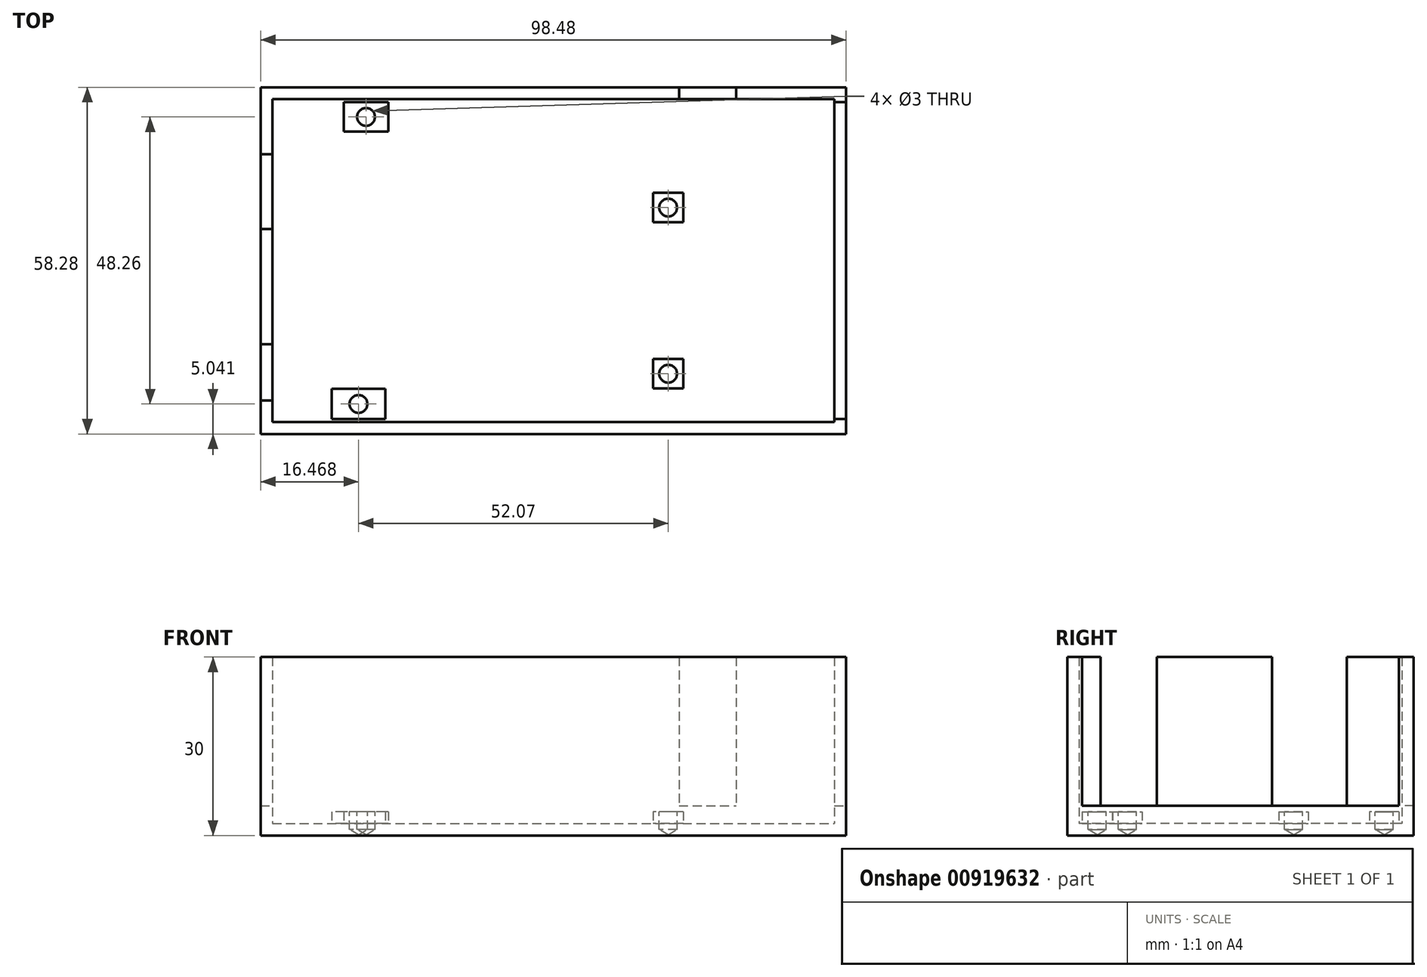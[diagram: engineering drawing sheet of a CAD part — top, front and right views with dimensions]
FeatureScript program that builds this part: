
annotation { "Feature Type Name" : "Feature", "Feature Type Description" : "" }
export const myFeature = defineFeature(function(context is Context, id is Id, definition is map)
    precondition{}
    {
        {
            var Q0;
            Q0=qCreatedBy(makeId("Top.planeOp"),FACE);
            var sketch = newSketch(context, id + "F0", { "sketchPlane" : qUnion([Q0])});
            skLineSegment(sketch, "E0.bottom", {"start": v(-55.82, 21.85) * mm, "end": v(38.66, 21.85) * mm});
            skLineSegment(sketch, "E0.top", {"start": v(-55.82, -32.43) * mm, "end": v(38.66, -32.43) * mm});
            skLineSegment(sketch, "E0.left", {"start": v(-55.82, 21.85) * mm, "end": v(-55.82, -32.43) * mm});
            skLineSegment(sketch, "E0.right", {"start": v(38.66, 21.85) * mm, "end": v(38.66, -32.43) * mm});
            skLineSegment(sketch, "E1.0", {"start": v(-57.82, 23.85) * mm, "end": v(40.66, 23.85) * mm});
            skLineSegment(sketch, "E1.1", {"start": v(-57.82, 23.85) * mm, "end": v(-57.82, -34.43) * mm});
            skLineSegment(sketch, "E1.2", {"start": v(-57.82, -34.43) * mm, "end": v(40.66, -34.43) * mm});
            skLineSegment(sketch, "E1.3", {"start": v(40.66, 23.85) * mm, "end": v(40.66, -34.43) * mm});
            skLineSegment(sketch, "E2", {"start": v(-57.82, 12.6) * mm, "end": v(-55.82, 12.6) * mm});
            skLineSegment(sketch, "E3", {"start": v(-57.82, 0) * mm, "end": v(-55.82, 0) * mm});
            skLineSegment(sketch, "E4", {"start": v(-57.82, -19.35) * mm, "end": v(-55.82, -19.35) * mm});
            skLineSegment(sketch, "E5", {"start": v(-57.82, -28.82) * mm, "end": v(-55.82, -28.82) * mm});
            skLineSegment(sketch, "E6", {"start": v(12.55, 23.85) * mm, "end": v(12.55, 21.85) * mm});
            skLineSegment(sketch, "E7", {"start": v(22.14, 21.85) * mm, "end": v(22.14, 23.85) * mm});
            skLineSegment(sketch, "E8", {"start": v(38.66, 21.35) * mm, "end": v(40.66, 21.35) * mm});
            skLineSegment(sketch, "E9", {"start": v(38.66, -31.93) * mm, "end": v(40.66, -31.93) * mm});
            skPoint(sketch, "E10", {"position": v(-40.08, 18.87) * mm});
            skLineSegment(sketch, "E11.bottom", {"start": v(-36.31, 21.35) * mm, "end": v(-43.85, 21.35) * mm});
            skLineSegment(sketch, "E11.top", {"start": v(-36.31, 16.4) * mm, "end": v(-43.85, 16.4) * mm});
            skLineSegment(sketch, "E11.left", {"start": v(-36.31, 21.35) * mm, "end": v(-36.31, 16.4) * mm});
            skLineSegment(sketch, "E11.right", {"start": v(-43.85, 21.35) * mm, "end": v(-43.85, 16.4) * mm});
            skPoint(sketch, "E12", {"position": v(-41.35, -29.39) * mm});
            skLineSegment(sketch, "E13.bottom", {"start": v(-36.84, -31.93) * mm, "end": v(-45.86, -31.93) * mm});
            skLineSegment(sketch, "E13.top", {"start": v(-36.84, -26.85) * mm, "end": v(-45.86, -26.85) * mm});
            skLineSegment(sketch, "E13.left", {"start": v(-36.84, -31.93) * mm, "end": v(-36.84, -26.85) * mm});
            skLineSegment(sketch, "E13.right", {"start": v(-45.86, -31.93) * mm, "end": v(-45.86, -26.85) * mm});
            skPoint(sketch, "E14", {"position": v(10.72, 3.63) * mm});
            skPoint(sketch, "E15", {"position": v(10.72, -24.3) * mm});
            skLineSegment(sketch, "E16.bottom", {"start": v(13.26, 1.14) * mm, "end": v(8.18, 1.14) * mm});
            skLineSegment(sketch, "E16.top", {"start": v(13.26, 6.12) * mm, "end": v(8.18, 6.12) * mm});
            skLineSegment(sketch, "E16.left", {"start": v(13.26, 1.14) * mm, "end": v(13.26, 6.12) * mm});
            skLineSegment(sketch, "E16.right", {"start": v(8.18, 1.14) * mm, "end": v(8.18, 6.12) * mm});
            skLineSegment(sketch, "E17.bottom", {"start": v(13.26, -26.8) * mm, "end": v(8.18, -26.8) * mm});
            skLineSegment(sketch, "E17.top", {"start": v(13.26, -21.82) * mm, "end": v(8.18, -21.82) * mm});
            skLineSegment(sketch, "E17.left", {"start": v(13.26, -26.8) * mm, "end": v(13.26, -21.82) * mm});
            skLineSegment(sketch, "E17.right", {"start": v(8.18, -26.8) * mm, "end": v(8.18, -21.82) * mm});
            skSolve(sketch);
        }
        {
            var Q0;
            {var subQ1=sQuery(id+"F0.wireOp",EDGE,"E0.top");Q0=makeQuery(id+"F0.imprint","IMPRINT",FACE,{"disambiguationData":[TD([[makeQuery(id+"F0.imprint","IMPRINT",EDGE,{"derivedFrom":subQ1}),1.0]])]});}
            extrude(context, id + "F1", {"entities" : qUnion([Q0]), "depth" : 2 * mm, "offsetDistance" : 25 * mm});
        }
        {
            var Q0;
            Q0=makeQuery(id+"F0.imprint","IMPRINT",FACE,{"disambiguationData":[TD([[makeQuery(id+"F0.imprint","IMPRINT",EDGE,{"derivedFrom":sQuery(id+"F0.wireOp",EDGE,"E11.bottom")}),1.0]])]});
            var Q1;
            Q1=makeQuery(id+"F0.imprint","IMPRINT",FACE,{"disambiguationData":[TD([[makeQuery(id+"F0.imprint","IMPRINT",EDGE,{"derivedFrom":sQuery(id+"F0.wireOp",EDGE,"E16.bottom")}),-1.0]])]});
            var Q2;
            Q2=makeQuery(id+"F0.imprint","IMPRINT",FACE,{"disambiguationData":[TD([[makeQuery(id+"F0.imprint","IMPRINT",EDGE,{"derivedFrom":sQuery(id+"F0.wireOp",EDGE,"E17.bottom")}),-1.0]])]});
            var Q3;
            Q3=makeQuery(id+"F0.imprint","IMPRINT",FACE,{"disambiguationData":[TD([[makeQuery(id+"F0.imprint","IMPRINT",EDGE,{"derivedFrom":sQuery(id+"F0.wireOp",EDGE,"E13.bottom")}),-1.0]])]});
            extrude(context, id + "F2", {"entities" : qUnion([Q0, Q1, Q2, Q3]), "operationType" : NewBodyOperationType.ADD, "depth" : 4 * mm, "offsetDistance" : 25 * mm});
        }
        {
            var Q0;
            Q0=makeQuery(id+"F2.opExtrude","CAP_FACE",FACE,{"disambiguationData":[OSD([sQuery(id+"F0.wireOp",EDGE,"E11.bottom"),sQuery(id+"F0.wireOp",EDGE,"E11.top"),sQuery(id+"F0.wireOp",EDGE,"E11.left"),sQuery(id+"F0.wireOp",EDGE,"E11.right")])],"isStart":false});
            var sketch = newSketch(context, id + "F3", { "sketchPlane" : qUnion([Q0])});
            skPoint(sketch, "E18.0", {"position": v(-40.08, 18.87) * mm});
            skPoint(sketch, "E19.0", {"position": v(-41.35, -29.39) * mm});
            skPoint(sketch, "E20.0", {"position": v(10.72, -24.3) * mm});
            skPoint(sketch, "E21.0", {"position": v(10.72, 3.63) * mm});
            skSolve(sketch);
        }
        {
            var Q0;
            Q0=sQuery(id+"F3.wireOp",VERTEX,"E18.0");
            var Q1;
            Q1=sQuery(id+"F3.wireOp",VERTEX,"E19.0");
            var Q2;
            Q2=sQuery(id+"F3.wireOp",VERTEX,"E20.0");
            var Q3;
            Q3=sQuery(id+"F3.wireOp",VERTEX,"E21.0");
            var Q4;
            Q4=makeQuery(id+"F1.opExtrude","SWEPT_BODY",BODY,{"disambiguationData":[OSD([sQuery(id+"F0.wireOp",EDGE,"E0.bottom"),sQuery(id+"F0.wireOp",EDGE,"E0.top"),sQuery(id+"F0.wireOp",EDGE,"E0.left"),sQuery(id+"F0.wireOp",EDGE,"E0.right"),sQuery(id+"F0.wireOp",EDGE,"E11.bottom"),sQuery(id+"F0.wireOp",EDGE,"E11.top"),sQuery(id+"F0.wireOp",EDGE,"E11.left"),sQuery(id+"F0.wireOp",EDGE,"E11.right"),sQuery(id+"F0.wireOp",EDGE,"E13.bottom"),sQuery(id+"F0.wireOp",EDGE,"E13.top"),sQuery(id+"F0.wireOp",EDGE,"E13.left"),sQuery(id+"F0.wireOp",EDGE,"E13.right"),sQuery(id+"F0.wireOp",EDGE,"E16.bottom"),sQuery(id+"F0.wireOp",EDGE,"E16.top"),sQuery(id+"F0.wireOp",EDGE,"E16.left"),sQuery(id+"F0.wireOp",EDGE,"E16.right"),sQuery(id+"F0.wireOp",EDGE,"E17.bottom"),sQuery(id+"F0.wireOp",EDGE,"E17.top"),sQuery(id+"F0.wireOp",EDGE,"E17.left"),sQuery(id+"F0.wireOp",EDGE,"E17.right")])]});
            hole(context, id + "F4", {"style" : HoleStyle.SIMPLE, "endStyle" : HoleEndStyle.BLIND, "holeDiameter" : 3 * mm, "majorDiameter" : 5 * mm, "holeDepth" : 3 * mm, "isTappedThrough" : true, "tappedDepth" : 12 * mm, "tapClearance" : 3, "locations" : qUnion([Q0, Q1, Q2, Q3]), "scope" : qUnion([Q4])});
        }
        {
            var Q0;
            {var subQ4=sQuery(id+"F0.wireOp",EDGE,"E0.top");Q0=makeQuery(id+"F0.imprint","IMPRINT",FACE,{"disambiguationData":[TD([[makeQuery(id+"F0.imprint","IMPRINT",EDGE,{"derivedFrom":subQ4}),-1.0]])]});}
            var Q1;
            {var subQ7=sQuery(id+"F0.wireOp",EDGE,"E2");Q1=makeQuery(id+"F0.imprint","IMPRINT",FACE,{"disambiguationData":[TD([[makeQuery(id+"F0.imprint","IMPRINT",EDGE,{"derivedFrom":subQ7}),1.0]])]});}
            var Q2;
            {var subQ0=sQuery(id+"F0.wireOp",EDGE,"E3");Q2=makeQuery(id+"F0.imprint","IMPRINT",FACE,{"disambiguationData":[TD([[makeQuery(id+"F0.imprint","IMPRINT",EDGE,{"derivedFrom":subQ0}),-1.0]])]});}
            var Q3;
            {var subQ4=sQuery(id+"F0.wireOp",EDGE,"E7");Q3=makeQuery(id+"F0.imprint","IMPRINT",FACE,{"disambiguationData":[TD([[makeQuery(id+"F0.imprint","IMPRINT",EDGE,{"derivedFrom":subQ4}),-1.0]])]});}
            extrude(context, id + "F5", {"entities" : qUnion([Q0, Q1, Q2, Q3]), "operationType" : NewBodyOperationType.ADD, "depth" : 30 * mm, "offsetDistance" : 25 * mm});
        }
        {
            var Q0;
            {var subQ0=sQuery(id+"F0.wireOp",EDGE,"E4");Q0=makeQuery(id+"F0.imprint","IMPRINT",FACE,{"disambiguationData":[TD([[makeQuery(id+"F0.imprint","IMPRINT",EDGE,{"derivedFrom":subQ0}),-1.0]])]});}
            var Q1;
            {var subQ0=sQuery(id+"F0.wireOp",EDGE,"E2");Q1=makeQuery(id+"F0.imprint","IMPRINT",FACE,{"disambiguationData":[TD([[makeQuery(id+"F0.imprint","IMPRINT",EDGE,{"derivedFrom":subQ0}),-1.0]])]});}
            var Q2;
            {var subQ0=sQuery(id+"F0.wireOp",EDGE,"E6");Q2=makeQuery(id+"F0.imprint","IMPRINT",FACE,{"disambiguationData":[TD([[makeQuery(id+"F0.imprint","IMPRINT",EDGE,{"derivedFrom":subQ0}),1.0]])]});}
            var Q3;
            {var subQ0=sQuery(id+"F0.wireOp",EDGE,"E8");Q3=makeQuery(id+"F0.imprint","IMPRINT",FACE,{"disambiguationData":[TD([[makeQuery(id+"F0.imprint","IMPRINT",EDGE,{"derivedFrom":subQ0}),-1.0]])]});}
            extrude(context, id + "F6", {"entities" : qUnion([Q0, Q1, Q2, Q3]), "operationType" : NewBodyOperationType.ADD, "depth" : 5 * mm, "offsetDistance" : 25 * mm});
        }
    });
